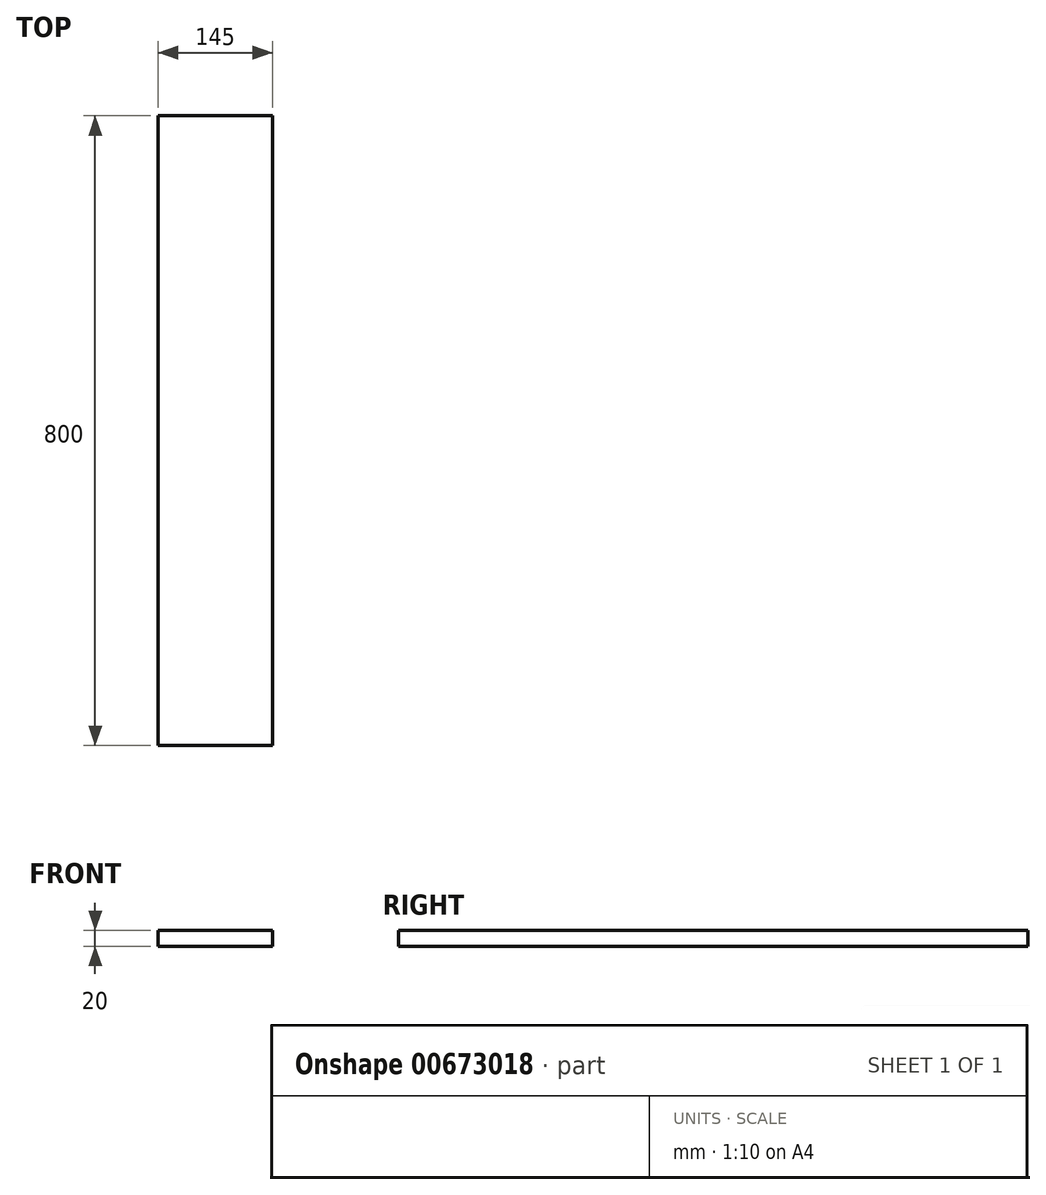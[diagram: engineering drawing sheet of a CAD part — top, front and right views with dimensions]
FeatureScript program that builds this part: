
annotation { "Feature Type Name" : "Feature", "Feature Type Description" : "" }
export const myFeature = defineFeature(function(context is Context, id is Id, definition is map)
    precondition{}
    {
        {
            var Q0;
            Q0=qCreatedBy(makeId("Front.planeOp"),FACE);
            var sketch = newSketch(context, id + "F0", { "sketchPlane" : qUnion([Q0])});
            skLineSegment(sketch, "E0.bottom", {"start": v(0, 0) * mm, "end": v(40.33, 0) * mm});
            skLineSegment(sketch, "E0.top", {"start": v(0, 25.44) * mm, "end": v(40.33, 25.44) * mm});
            skLineSegment(sketch, "E0.left", {"start": v(0, 0) * mm, "end": v(0, 25.44) * mm});
            skLineSegment(sketch, "E0.right", {"start": v(40.33, 0) * mm, "end": v(40.33, 25.44) * mm});
            skSolve(sketch);
        }
        {
            var Q0;
            Q0=makeQuery(id+"F0.imprint","IMPRINT",FACE,{"disambiguationData":[TD([[makeQuery(id+"F0.imprint","IMPRINT",EDGE,{"derivedFrom":sQuery(id+"F0.wireOp",EDGE,"E0.bottom")}),1.0]])]});
            extrude(context, id + "F1", {"entities" : qUnion([Q0]), "depth" : 800 * mm, "offsetDistance" : 25 * mm});
        }
        {
            var Q0;
            Q0=makeQuery(id+"F1.opExtrude","SWEPT_FACE",FACE,{"disambiguationData":[OSD([sQuery(id+"F0.wireOp",EDGE,"E0.bottom")])]});
            extrude(context, id + "F2", {"entities" : qUnion([Q0]), "operationType" : NewBodyOperationType.INTERSECT, "oppositeDirection" : true, "depth" : 20 * mm, "offsetDistance" : 25 * mm});
        }
        {
            var Q0;
            Q0=makeQuery(id+"F1.opExtrude","SWEPT_FACE",FACE,{"disambiguationData":[OSD([sQuery(id+"F0.wireOp",EDGE,"E0.left")])]});
            extrude(context, id + "F3", {"entities" : qUnion([Q0]), "operationType" : NewBodyOperationType.ADD, "oppositeDirection" : true, "depth" : 25 * mm, "offsetDistance" : 25 * mm});
        }
        {
            var Q0;
            Q0=makeQuery(id+"F1.opExtrude","SWEPT_FACE",FACE,{"disambiguationData":[OSD([sQuery(id+"F0.wireOp",EDGE,"E0.left")])]});
            extrude(context, id + "F4", {"entities" : qUnion([Q0]), "operationType" : NewBodyOperationType.ADD, "oppositeDirection" : true, "depth" : 145 * mm, "offsetDistance" : 25 * mm});
        }
    });
